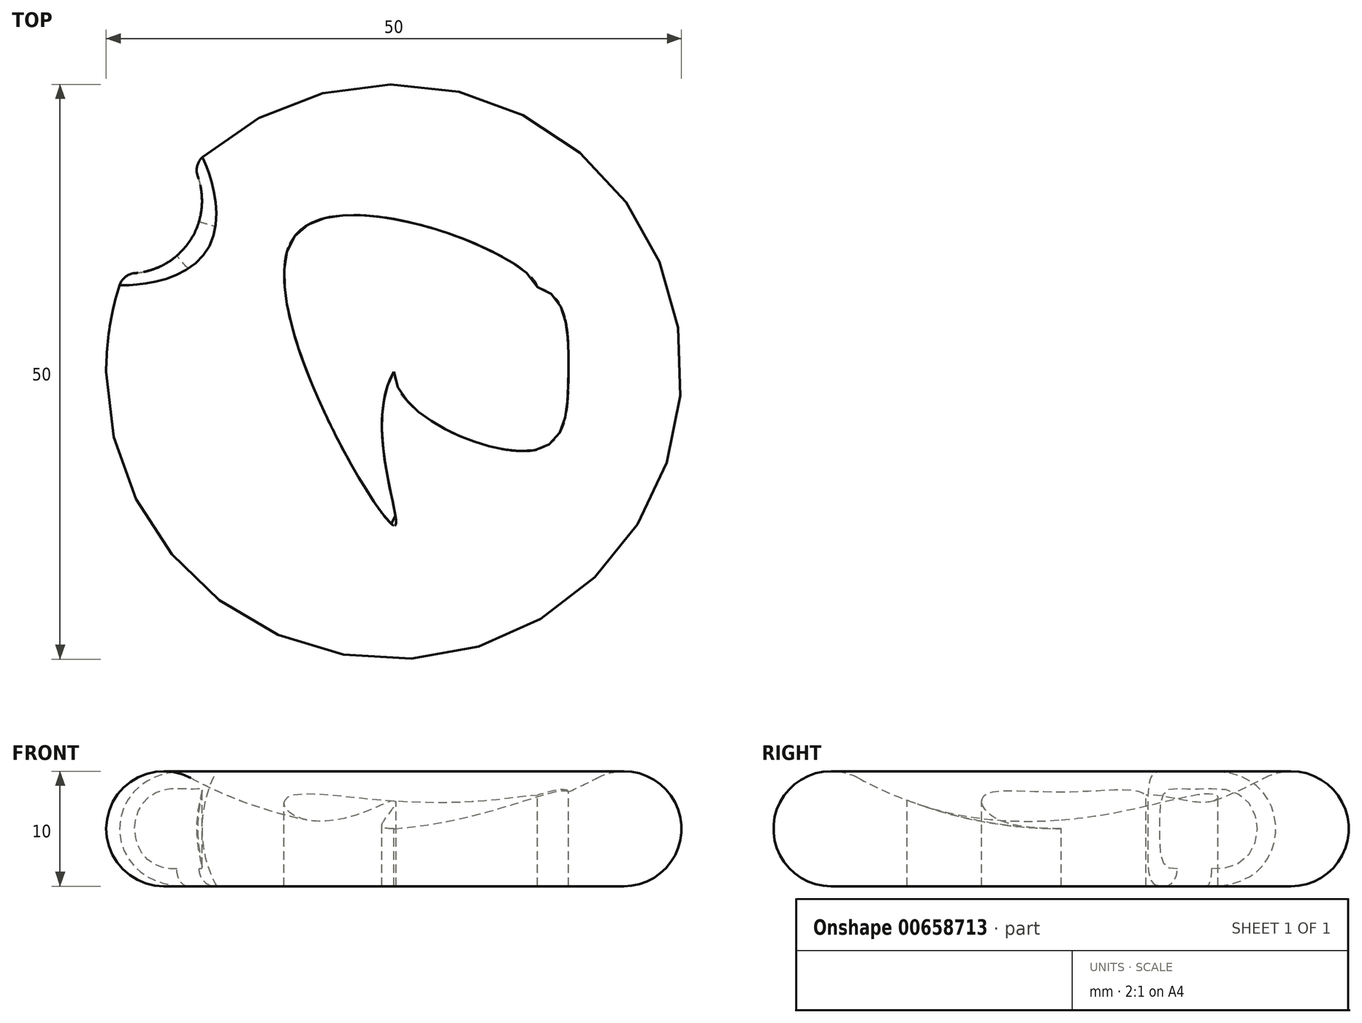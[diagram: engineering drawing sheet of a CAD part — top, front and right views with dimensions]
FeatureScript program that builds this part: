
annotation { "Feature Type Name" : "Feature", "Feature Type Description" : "" }
export const myFeature = defineFeature(function(context is Context, id is Id, definition is map)
    precondition{}
    {
        {
            var Q0;
            Q0=qCreatedBy(makeId("Front.planeOp"),FACE);
            var sketch = newSketch(context, id + "F0", { "sketchPlane" : qUnion([Q0])});
            skArc(sketch, "E0", {"start": v(-17.65, 9.41) * mm, "mid": v(-9.1, 6.12) * mm, "end": v(0, 5) * mm});
            skCircle(sketch, "E1", {"center": v(-20, 5) * mm, "radius": 5 * mm});
            skLineSegment(sketch, "E2", {"start": v(-20, 0) * mm, "end": v(0, 0) * mm});
            skLineSegment(sketch, "E3", {"start": v(0, 0) * mm, "end": v(0, 5) * mm});
            skSolve(sketch);
        }
        {
            var Q0;
            Q0 = qSketchRegion(id + "F0", true);
            var Q1;
            Q1=sQuery(id+"F0.wireOp",EDGE,"E3");
            revolve(context, id + "F1", {"entities" : qUnion([Q0]), "axis" : qUnion([Q1]), "revolveType" : RevolveType.FULL});
        }
        {
            var Q0;
            Q0=qCreatedBy(makeId("Top.planeOp"),FACE);
            cPlane(context, id + "F2", {"entities" : qUnion([Q0]), "cplaneType" : CPlaneType.OFFSET, "offset" : 10 * mm, "width" : 150 * mm, "height" : 150 * mm});
        }
        {
            var Q0;
            Q0=qCreatedBy(id+"F2.planeOp",FACE);
            var sketch = newSketch(context, id + "F3", { "sketchPlane" : qUnion([Q0])});
            skCircle(sketch, "E4", {"center": v(0, 0) * mm, "radius": 7 * mm});
            skCircle(sketch, "E5", {"center": v(-8.8, 10.89) * mm, "radius": 7 * mm});
            skCircle(sketch, "E6", {"center": v(11.48, 7.8) * mm, "radius": 7 * mm});
            skCircle(sketch, "E7", {"center": v(0, -13.18) * mm, "radius": 7 * mm});
            skSolve(sketch);
        }
        {
            var Q0;
            Q0 = qSketchRegion(id + "F3", true);
            extrude(context, id + "F4", {"entities" : qUnion([Q0]), "operationType" : NewBodyOperationType.REMOVE, "depth" : 25 * mm, "offsetDistance" : 25 * mm});
        }
        {
            var Q0;
            Q0=qCreatedBy(id+"F2.planeOp",FACE);
            var sketch = newSketch(context, id + "F5", { "sketchPlane" : qUnion([Q0])});
            skFitSpline(sketch, "E8", {"points": [v(-8.57, 11.87) * mm, v(12.47, 7.36) * mm, v(0, 0) * mm, v(0, -13.38) * mm, v(-8.57, 11.87) * mm]});
            skFitSpline(sketch, "E9", {"points": [v(0, 0) * mm, v(12.47, -6.76) * mm, v(15.18, 0) * mm, v(12.47, 7.36) * mm, v(0, 0) * mm]});
            skSolve(sketch);
        }
        {
            var Q0;
            Q0 = qSketchRegion(id + "F5", true);
            extrude(context, id + "F6", {"entities" : qUnion([Q0]), "operationType" : NewBodyOperationType.REMOVE, "oppositeDirection" : true, "depth" : 25 * mm, "offsetDistance" : 25 * mm});
        }
        {
            var Q0;
            Q0=qCreatedBy(id+"F2.planeOp",FACE);
            var sketch = newSketch(context, id + "F7", { "sketchPlane" : qUnion([Q0])});
            skCircle(sketch, "E10", {"center": v(-23, 14.88) * mm, "radius": 6.32 * mm});
            skSolve(sketch);
        }
        {
            var Q0;
            Q0 = qSketchRegion(id + "F7", true);
            extrude(context, id + "F8", {"entities" : qUnion([Q0]), "operationType" : NewBodyOperationType.REMOVE, "oppositeDirection" : true, "depth" : 25 * mm, "offsetDistance" : 25 * mm});
        }
        {
            var Q0;
            Q0=makeQuery(id+"F8.boolean.opBoolean","INTERSECT",EDGE,{"derivedFrom":[makeQuery(id+"F1.opRevolve","SWEPT_FACE",FACE,{"disambiguationData":[OSD([sQuery(id+"F0.wireOp",EDGE,"E1")])]}),makeQuery(id+"F8.opExtrude","SWEPT_FACE",FACE,{"disambiguationData":[OSD([sQuery(id+"F7.wireOp",EDGE,"E10")])]})]});
            fillet(context, id + "F9", {"entities" : qUnion([Q0]), "radius" : 1.5 * mm, "tangentPropagation" : true, "allowEdgeOverflow" : false});
        }
    });
